# Revit family: Building-FlushMountingEnclosures-GEWISS-48CM-GREENWALL-JUNCTION-BOXES_FLUSH-MOUNTING_HIGH_CAPACITY
name_source: partatom
category: Apparecchi elettrici
revit_build: Autodesk Revit 2016 (Build: 20161004_0715(x64)
units: mm (PartAtom-declared; Revit-internal decimal feet)

## family parameters
Condiviso = No
Host = Superficie
Mantenere orientamento annotazione = Sì
Numero OmniClass = 23.80.30.14.24
Punto di calcolo locali = Sì
Quota connettore circolare = Usa diametro
Taglio con vuoti quando caricato = No
Tipo di parte = Normale
Titolo OmniClass = Junction Boxes

## types (2) — shared parameters
Bordo = 4 mm  [stored 0.0131234 ft]
Carico apparente = 0 VA
Catalogue = BUILDING
Catalogue Range = 48 CM
Classificazione = Other
Electrocod = 0220
For walls = Plasterboard
GEWISS SCHEDA TECNICA = http://pro.gewiss.com
Glow Wire Test = 850°C
IDF = 2e85a4a3-2cd7-4bb8-b581-491810878a2a
IDT = 02828416-875e-45d8-8135-fffb5b53fa53
IP degree = IP40
Immagine tipo = GW48211PM.jpg
Installation = Flush mounting enclosures
Larghezza = 260 mm  [stored 0.853018 ft]
Lid colour = White RAL 9016
Lunghezza = 520 mm  [stored 1.70604 ft]
Operating temperature = -15 ÷ +60°C
Produttore = GEWISS S.p.A.
Profondità = 121 mm  [stored 0.396982 ft]
Prospetto di default = 1219 mm
SEO = Box
Scatola = GEWISS - scatola a incasso
Shock resistance = IK07
Tappo = GEWISS - BIANCO RAL 9016
Technical sheet = https://www.gewiss.com
Type of material = Halogen-free in compliance with EN 60754-2
URL = https://www.gewiss.com
Version file RFA = 18.0
Voltaggio = 0 V

## per-type parameters (varying)
| type | Compartment pre-arrangement | Descrizione | Dispersible max power (W) | Dispersible power (W) | EAN code | Modello | Outer dim. LxHxD (mm) |
| GW48207PM - UPRIGHTS P.B. BOX 260X260X121 PLAIN LID | 2 | UPRIGHTS P.B. BOX 260X260X121 PLAIN LID | 13 | 13 | 8011564801110 | GW48207PM | 260x260x121 |
| GW48211PM - UPRIGHTS P.B. BOX 520X260X121 PLAIN LID | 5 | UPRIGHTS P.B. BOX 520X260X121 PLAIN LID | 30 | 30 | 8011564801127 | GW48211PM | 520x260x121 |

note: [stored X ft] marks values corroborated as IEEE doubles in the binary element streams (Revit-internal decimal feet)

## geometry (parser evidence)
native form markers: Blend x2, Sweep x2
no freeform markers — native parametric forms only
